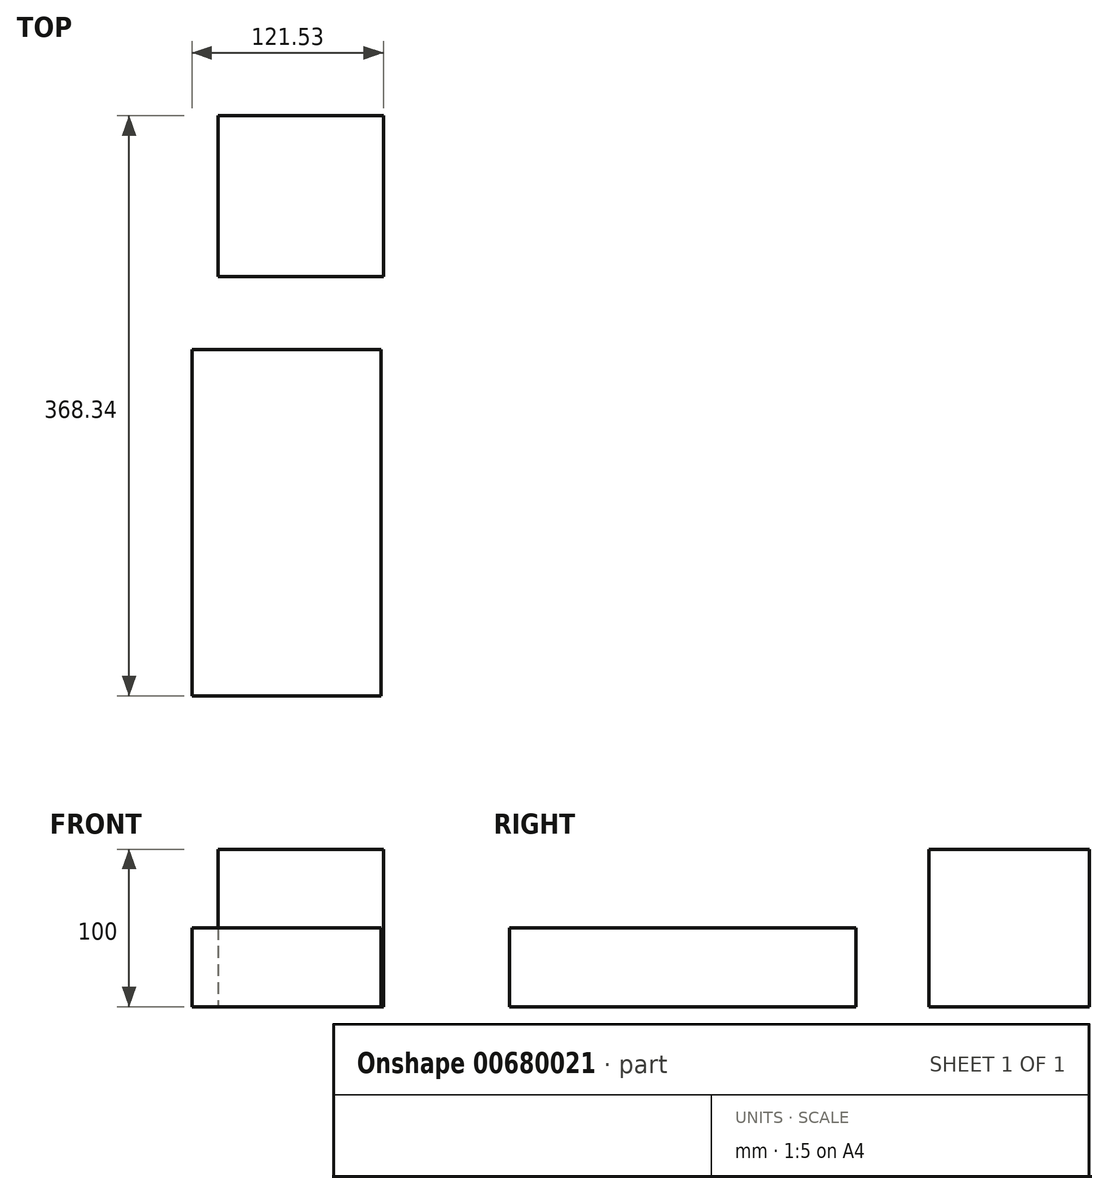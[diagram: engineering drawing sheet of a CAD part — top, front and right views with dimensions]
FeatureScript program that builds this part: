
annotation { "Feature Type Name" : "Feature", "Feature Type Description" : "" }
export const myFeature = defineFeature(function(context is Context, id is Id, definition is map)
    precondition{}
    {
        {
            var Q0;
            Q0=qCreatedBy(makeId("Top.planeOp"),FACE);
            var sketch = newSketch(context, id + "F0", { "sketchPlane" : qUnion([Q0])});
            skLineSegment(sketch, "E0", {"start": v(43.65, 16.56) * mm, "end": v(148.65, 16.56) * mm});
            skLineSegment(sketch, "E1", {"start": v(148.65, 16.56) * mm, "end": v(148.65, 118.56) * mm});
            skLineSegment(sketch, "E2", {"start": v(148.65, 118.56) * mm, "end": v(43.65, 118.56) * mm});
            skLineSegment(sketch, "E3", {"start": v(43.65, 118.56) * mm, "end": v(43.65, 16.56) * mm});
            skSolve(sketch);
        }
        {
            var Q0;
            Q0=qSketchRegion(id+"F0",true);
            extrude(context, id + "F1", {"entities" : qUnion([Q0]), "depth" : 100 * mm});
        }
        {
            var Q0;
            Q0=qCreatedBy(makeId("Top.planeOp"),FACE);
            var sketch = newSketch(context, id + "F2", { "sketchPlane" : qUnion([Q0])});
            skLineSegment(sketch, "E4.rect.bottom", {"start": v(147.12, -249.78) * mm, "end": v(27.12, -249.78) * mm});
            skLineSegment(sketch, "E4.rect.top", {"start": v(147.12, -29.78) * mm, "end": v(27.12, -29.78) * mm});
            skLineSegment(sketch, "E4.rect.left", {"start": v(147.12, -249.78) * mm, "end": v(147.12, -29.78) * mm});
            skLineSegment(sketch, "E4.rect.right", {"start": v(27.12, -249.78) * mm, "end": v(27.12, -29.78) * mm});
            skPoint(sketch, "E4.rect.middle", {"position": v(87.12, -139.78) * mm});
            skSolve(sketch);
        }
        {
            var Q0;
            Q0=qSketchRegion(id+"F2",true);
            extrude(context, id + "F3", {"entities" : qUnion([Q0]), "depth" : 50 * mm});
        }
    });
